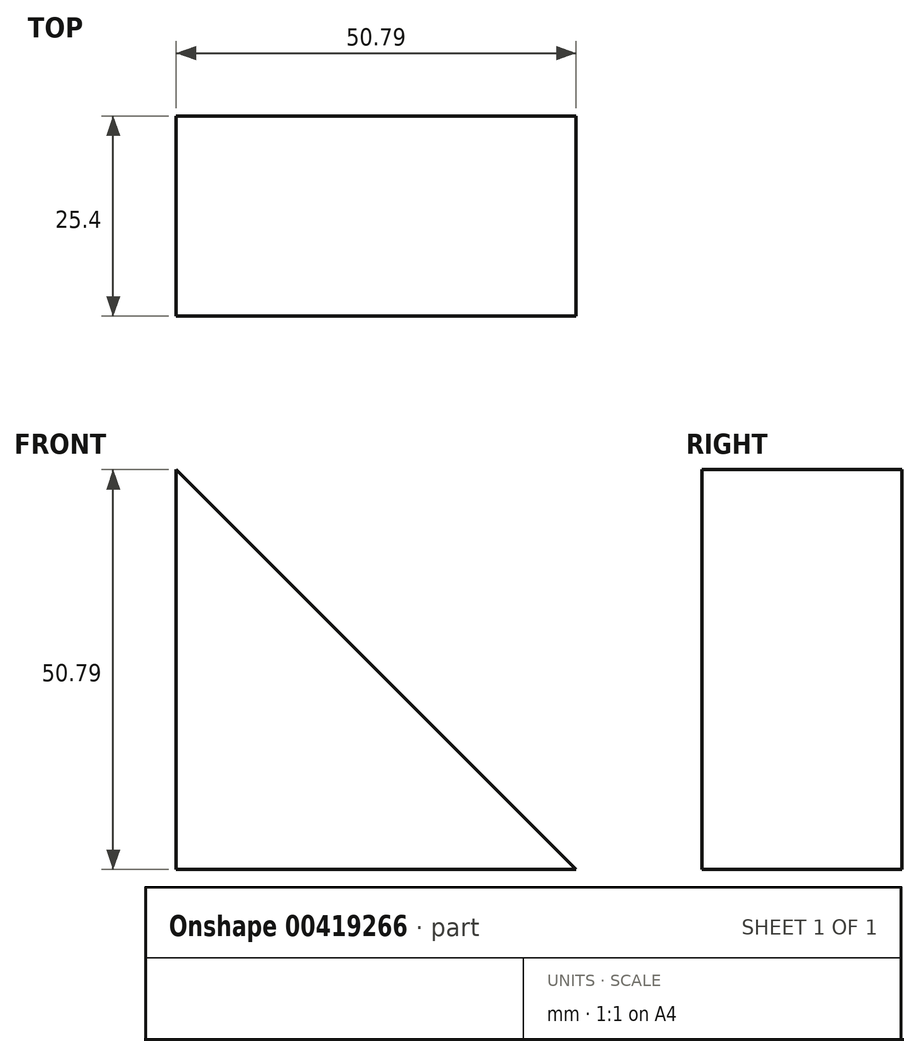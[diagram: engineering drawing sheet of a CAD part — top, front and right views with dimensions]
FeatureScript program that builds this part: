
annotation { "Feature Type Name" : "Feature", "Feature Type Description" : "" }
export const myFeature = defineFeature(function(context is Context, id is Id, definition is map)
    precondition{}
    {
        {
            var Q0;
            Q0=qCreatedBy(makeId("Front.planeOp"),FACE);
            var sketch = newSketch(context, id + "F0", { "sketchPlane" : qUnion([Q0])});
            skLineSegment(sketch, "E0", {"start": v(0, 0) * mm, "end": v(-50.8, 0) * mm});
            skLineSegment(sketch, "E1", {"start": v(-50.8, 0) * mm, "end": v(-50.8, 50.8) * mm});
            skLineSegment(sketch, "E2", {"start": v(-50.8, 50.8) * mm, "end": v(0, 0) * mm});
            skSolve(sketch);
        }
        {
            var Q0;
            Q0=makeQuery(id+"F0.imprint","IMPRINT",FACE,{"disambiguationData":[TD([[makeQuery(id+"F0.imprint","IMPRINT",EDGE,{"derivedFrom":sQuery(id+"F0.wireOp",EDGE,"E0")}),-1.0]])]});
            extrude(context, id + "F1", {"entities" : qUnion([Q0]), "depth" : 25.4 * mm});
        }
    });
